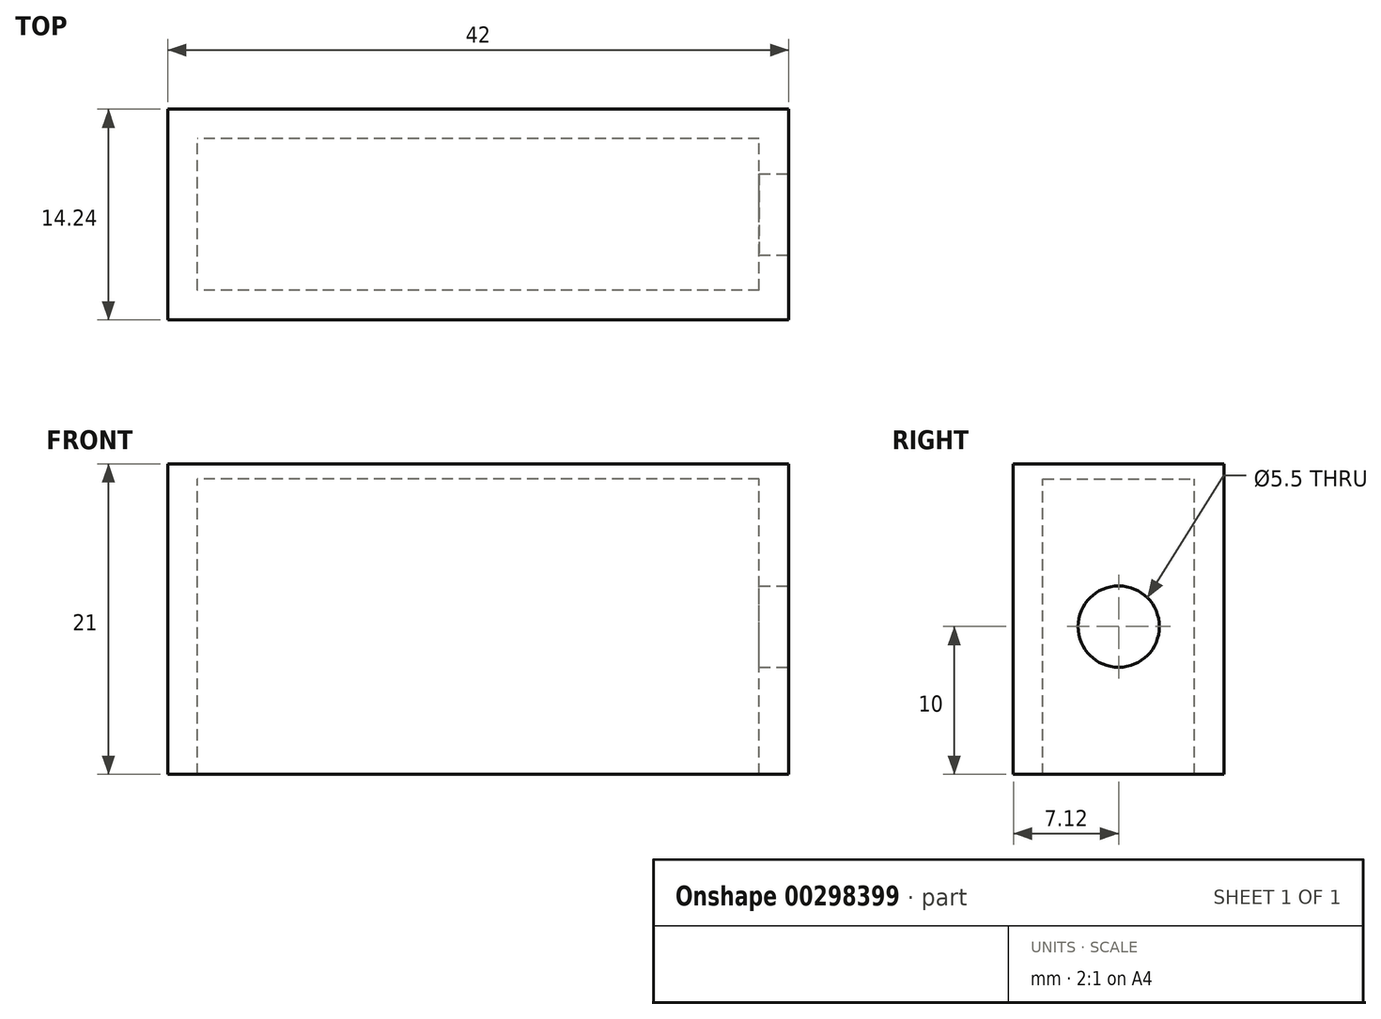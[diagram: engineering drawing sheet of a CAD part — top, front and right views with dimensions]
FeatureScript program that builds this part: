
annotation { "Feature Type Name" : "Feature", "Feature Type Description" : "" }
export const myFeature = defineFeature(function(context is Context, id is Id, definition is map)
    precondition{}
    {
        {
            var Q0;
            Q0=qCreatedBy(makeId("Top.planeOp"),FACE);
            var sketch = newSketch(context, id + "F0", { "sketchPlane" : qUnion([Q0])});
            skLineSegment(sketch, "E0.bottom", {"start": v(19, -5.12) * mm, "end": v(-19, -5.13) * mm});
            skLineSegment(sketch, "E0.top", {"start": v(19, 5.12) * mm, "end": v(-19, 5.12) * mm});
            skLineSegment(sketch, "E0.left", {"start": v(19, -5.12) * mm, "end": v(19, 5.13) * mm});
            skLineSegment(sketch, "E0.right", {"start": v(-19, -5.13) * mm, "end": v(-19, 5.13) * mm});
            skPoint(sketch, "E0.middle", {"position": v(0, 0) * mm});
            skLineSegment(sketch, "E1.bottom", {"start": v(21, -7.12) * mm, "end": v(-21, -7.13) * mm});
            skLineSegment(sketch, "E1.top", {"start": v(21, 7.13) * mm, "end": v(-21, 7.12) * mm});
            skLineSegment(sketch, "E1.left", {"start": v(21, -7.13) * mm, "end": v(21, 7.12) * mm});
            skLineSegment(sketch, "E1.right", {"start": v(-21, -7.12) * mm, "end": v(-21, 7.13) * mm});
            skSolve(sketch);
        }
        {
            var Q0;
            Q0 = qSketchRegion(id + "F0", true);
            var Q1;
            Q1=makeQuery(id+"F0.imprint","IMPRINT",FACE,{"disambiguationData":[TD([[makeQuery(id+"F0.imprint","IMPRINT",EDGE,{"derivedFrom":sQuery(id+"F0.wireOp",EDGE,"E0.bottom")}),-1.0]])]});
            extrude(context, id + "F1", {"entities" : qUnion([Q0, Q1]), "depth" : 1 * mm});
        }
        {
            var Q0;
            Q0=makeQuery(id+"F0.imprint","IMPRINT",FACE,{"disambiguationData":[TD([[makeQuery(id+"F0.imprint","IMPRINT",EDGE,{"derivedFrom":sQuery(id+"F0.wireOp",EDGE,"E0.bottom")}),1.0]])]});
            extrude(context, id + "F2", {"entities" : qUnion([Q0]), "operationType" : NewBodyOperationType.ADD, "oppositeDirection" : true, "depth" : 20 * mm});
        }
        {
            var Q0;
            {var subQ0=sQuery(id+"F0.wireOp",EDGE,"E1.left");Q0=makeQuery(id+"F2.boolean.opBoolean","MERGE",FACE,{"derivedFrom":[makeQuery(id+"F1.opExtrude","SWEPT_FACE",FACE,{"disambiguationData":[OSD([subQ0])]}),makeQuery(id+"F2.opExtrude","SWEPT_FACE",FACE,{"disambiguationData":[OSD([subQ0])]})]});}
            var sketch = newSketch(context, id + "F3", { "sketchPlane" : qUnion([Q0])});
            skPoint(sketch, "E2", {"position": v(0, -10) * mm});
            skSolve(sketch);
        }
        {
            var Q0;
            Q0=sQuery(id+"F3.wireOp",VERTEX,"E2");
            var Q1;
            Q1=makeQuery(id+"F1.opExtrude","SWEPT_BODY",BODY,{"disambiguationData":[OSD([sQuery(id+"F0.wireOp",EDGE,"E1.bottom"),sQuery(id+"F0.wireOp",EDGE,"E1.top"),sQuery(id+"F0.wireOp",EDGE,"E1.left"),sQuery(id+"F0.wireOp",EDGE,"E1.right")])]});
            hole(context, id + "F4", {"style" : HoleStyle.SIMPLE, "endStyle" : HoleEndStyle.BLIND, "holeDiameter" : 5.5 * mm, "holeDepth" : 14.4 * mm, "tappedDepth" : 12 * mm, "tapClearance" : 3, "locations" : qUnion([Q0]), "scope" : qUnion([Q1])});
        }
    });
